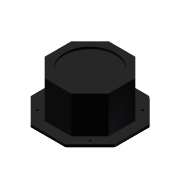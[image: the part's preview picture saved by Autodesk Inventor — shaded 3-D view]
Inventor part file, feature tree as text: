
AUTODESK INVENTOR PART (.ipt)
format: ipt  version: 2012 (Build 160160000, 160)  size: 124,416 bytes
history: native  units: mm
features: extrude x3, sketch x2
ambient origin geometry x8: Origin, YZ Plane, XZ Plane, XY Plane, X Axis, Y Axis, Z Axis, Center Point
bodies: Solid1 (feature_tree)
feature tree (5):
  sketch  "Sketch1"  dims[d0=4.7625mm d1=0.0mm d2=89.0mm d3=0.0mm]
  extrude  "Extrusion1"  Depth=89.0mm TaperAngle=0.0deg
  extrude  "Extrusion2"  [1 undecoded]
  extrude  "Extrusion3"  [1 undecoded]
  sketch  "Sketch2"  dims[d4=4.7625mm d5=0.0mm]
note: 2 required parameter values undecoded (feature->parameter linkage not recoverable at this tier; creation-order binding heuristic only, values carry confidence <= 0.55)
